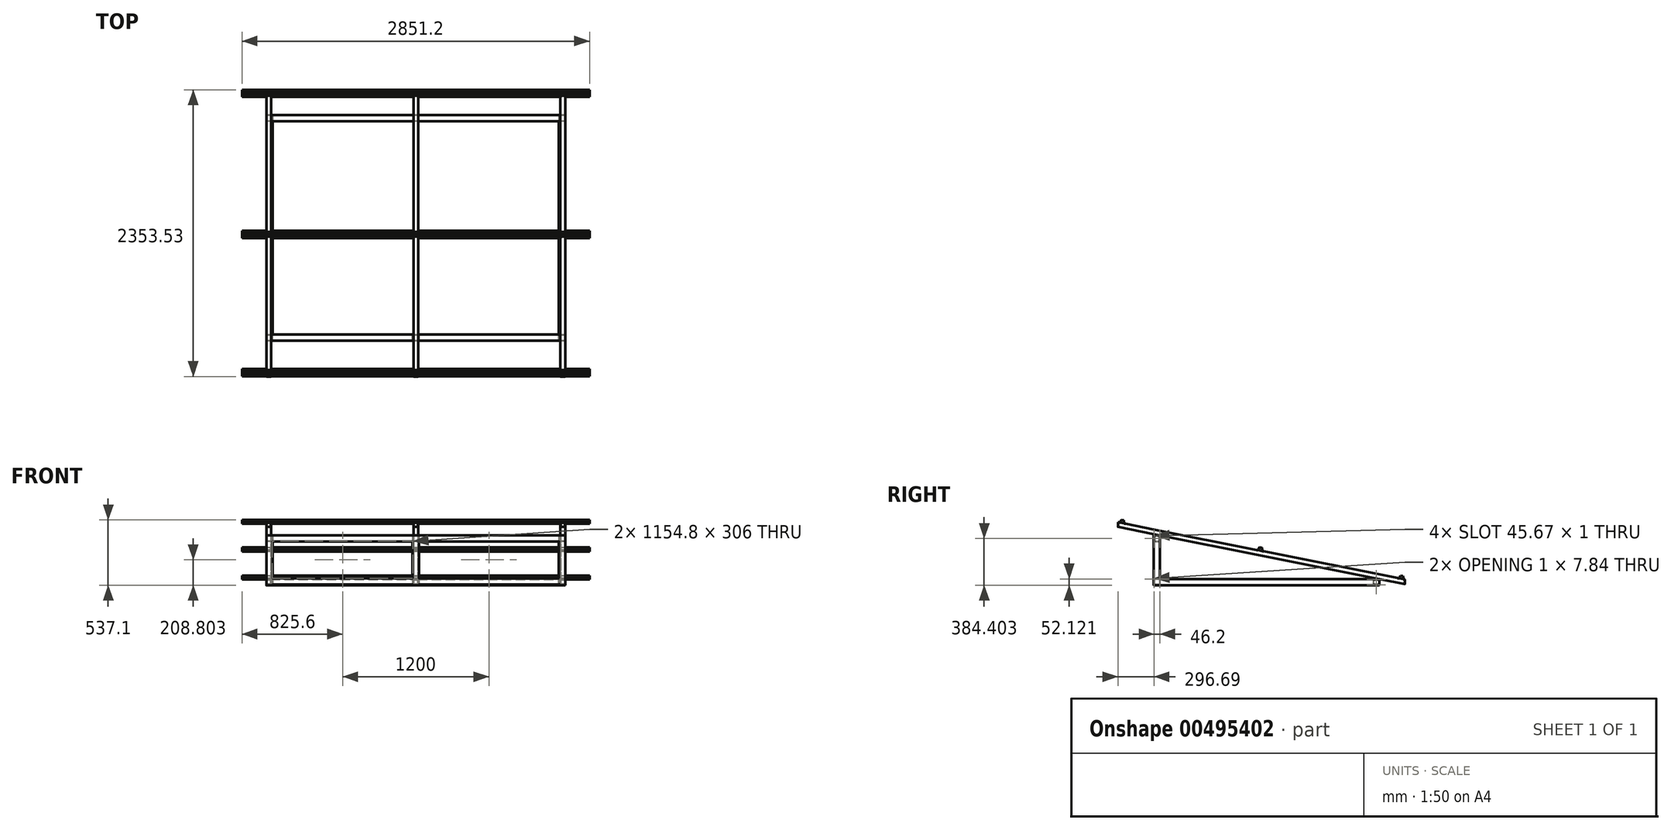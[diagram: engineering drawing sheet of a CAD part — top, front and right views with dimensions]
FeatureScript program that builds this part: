
annotation { "Feature Type Name" : "Feature", "Feature Type Description" : "" }
export const myFeature = defineFeature(function(context is Context, id is Id, definition is map)
    precondition{}
    {
        {
            var Q0;
            Q0=qCreatedBy(makeId("Front.planeOp"),FACE);
            var sketch = newSketch(context, id + "F0", { "sketchPlane" : qUnion([Q0])});
            skLineSegment(sketch, "E0.bottom", {"start": v(-48.2, -14.68) * mm, "end": v(-3, -14.68) * mm});
            skLineSegment(sketch, "E0.top", {"start": v(-48.2, 36.52) * mm, "end": v(-3, 36.52) * mm});
            skLineSegment(sketch, "E0.left", {"start": v(-51.2, -11.68) * mm, "end": v(-51.2, 33.52) * mm});
            skLineSegment(sketch, "E0.right", {"start": v(0, -11.68) * mm, "end": v(0, 33.52) * mm});
            skLineSegment(sketch, "E1.0", {"start": v(-49.2, -9.68) * mm, "end": v(-49.2, 31.52) * mm});
            skLineSegment(sketch, "E1.1", {"start": v(-46.2, -12.68) * mm, "end": v(-5, -12.68) * mm});
            skLineSegment(sketch, "E1.2", {"start": v(-2, -9.68) * mm, "end": v(-2, 31.52) * mm});
            skLineSegment(sketch, "E1.3", {"start": v(-46.2, 34.52) * mm, "end": v(-5, 34.52) * mm});
            skPoint(sketch, "E2.visualSharp", {"position": v(-49.2, 34.52) * mm});
            skArc(sketch, "E2.filletArc", {"start": v(-46.2, 34.52) * mm, "mid": v(-48.32, 33.64) * mm, "end": v(-49.2, 31.52) * mm});
            skPoint(sketch, "E3.visualSharp", {"position": v(-2, 34.52) * mm});
            skArc(sketch, "E3.filletArc", {"start": v(-2, 31.52) * mm, "mid": v(-2.88, 33.64) * mm, "end": v(-5, 34.52) * mm});
            skPoint(sketch, "E4.visualSharp", {"position": v(-2, -12.68) * mm});
            skArc(sketch, "E4.filletArc", {"start": v(-5, -12.68) * mm, "mid": v(-2.88, -11.8) * mm, "end": v(-2, -9.68) * mm});
            skPoint(sketch, "E5.visualSharp", {"position": v(-49.2, -12.68) * mm});
            skArc(sketch, "E5.filletArc", {"start": v(-49.2, -9.68) * mm, "mid": v(-48.32, -11.8) * mm, "end": v(-46.2, -12.68) * mm});
            skPoint(sketch, "E6.visualSharp", {"position": v(-51.2, -14.68) * mm});
            skArc(sketch, "E6.filletArc", {"start": v(-51.2, -11.68) * mm, "mid": v(-50.32, -13.8) * mm, "end": v(-48.2, -14.68) * mm});
            skPoint(sketch, "E7.visualSharp", {"position": v(-51.2, 36.52) * mm});
            skArc(sketch, "E7.filletArc", {"start": v(-48.2, 36.52) * mm, "mid": v(-50.32, 35.64) * mm, "end": v(-51.2, 33.52) * mm});
            skPoint(sketch, "E8.visualSharp", {"position": v(0, 36.52) * mm});
            skArc(sketch, "E8.filletArc", {"start": v(0, 33.52) * mm, "mid": v(-0.88, 35.64) * mm, "end": v(-3, 36.52) * mm});
            skPoint(sketch, "E9.visualSharp", {"position": v(0, -14.68) * mm});
            skArc(sketch, "E9.filletArc", {"start": v(-3, -14.68) * mm, "mid": v(-0.88, -13.8) * mm, "end": v(0, -11.68) * mm});
            skLineSegment(sketch, "E10", {"start": v(-51.2, 10.92) * mm, "end": v(0, 10.92) * mm});
            skLineSegment(sketch, "E11", {"start": v(-25.6, 10.92) * mm, "end": v(-25.6, 36.52) * mm});
            skLineSegment(sketch, "E12.1.0.0", {"start": v(2351.8, 36.52) * mm, "end": v(2397, 36.52) * mm});
            skArc(sketch, "E12.1.0.1", {"start": v(2400, 33.52) * mm, "mid": v(2399.12, 35.64) * mm, "end": v(2397, 36.52) * mm});
            skArc(sketch, "E12.1.0.2", {"start": v(2398, 31.52) * mm, "mid": v(2397.12, 33.64) * mm, "end": v(2395, 34.52) * mm});
            skLineSegment(sketch, "E12.1.0.3", {"start": v(2400, -11.68) * mm, "end": v(2400, 33.52) * mm});
            skLineSegment(sketch, "E12.1.0.4", {"start": v(2398, -9.68) * mm, "end": v(2398, 31.52) * mm});
            skLineSegment(sketch, "E12.1.0.5", {"start": v(2353.8, 34.52) * mm, "end": v(2395, 34.52) * mm});
            skArc(sketch, "E12.1.0.6", {"start": v(2353.8, 34.52) * mm, "mid": v(2351.68, 33.64) * mm, "end": v(2350.8, 31.52) * mm});
            skArc(sketch, "E12.1.0.7", {"start": v(2351.8, 36.52) * mm, "mid": v(2349.68, 35.64) * mm, "end": v(2348.8, 33.52) * mm});
            skLineSegment(sketch, "E12.1.0.8", {"start": v(2348.8, -11.68) * mm, "end": v(2348.8, 33.52) * mm});
            skLineSegment(sketch, "E12.1.0.9", {"start": v(2350.8, -9.68) * mm, "end": v(2350.8, 31.52) * mm});
            skArc(sketch, "E12.1.0.10", {"start": v(2350.8, -9.68) * mm, "mid": v(2351.68, -11.8) * mm, "end": v(2353.8, -12.68) * mm});
            skArc(sketch, "E12.1.0.11", {"start": v(2348.8, -11.68) * mm, "mid": v(2349.68, -13.8) * mm, "end": v(2351.8, -14.68) * mm});
            skLineSegment(sketch, "E12.1.0.12", {"start": v(2353.8, -12.68) * mm, "end": v(2395, -12.68) * mm});
            skLineSegment(sketch, "E12.1.0.13", {"start": v(2351.8, -14.68) * mm, "end": v(2397, -14.68) * mm});
            skArc(sketch, "E12.1.0.14", {"start": v(2395, -12.68) * mm, "mid": v(2397.12, -11.8) * mm, "end": v(2398, -9.68) * mm});
            skArc(sketch, "E12.1.0.15", {"start": v(2397, -14.68) * mm, "mid": v(2399.12, -13.8) * mm, "end": v(2400, -11.68) * mm});
            skLineSegment(sketch, "E12.direction1", {"start": v(-48.2, 36.52) * mm, "end": v(2351.8, 36.52) * mm, "construction": true});
            skSolve(sketch);
        }
        {
            var Q0;
            {var subQ0=sQuery(id+"F0.wireOp",EDGE,"E3.filletArc");Q0=makeQuery(id+"F0.imprint","IMPRINT",FACE,{"disambiguationData":[TD([[makeQuery(id+"F0.imprint","IMPRINT",EDGE,{"derivedFrom":subQ0}),-1.0]])]});}
            var Q1;
            {var subQ0=sQuery(id+"F0.wireOp",EDGE,"E2.filletArc");Q1=makeQuery(id+"F0.imprint","IMPRINT",FACE,{"disambiguationData":[TD([[makeQuery(id+"F0.imprint","IMPRINT",EDGE,{"derivedFrom":subQ0}),-1.0]])]});}
            var Q2;
            Q2=makeQuery(id+"F0.imprint","IMPRINT",FACE,{"disambiguationData":[TD([[makeQuery(id+"F0.imprint","IMPRINT",EDGE,{"derivedFrom":sQuery(id+"F0.wireOp",EDGE,"E0.bottom")}),1.0]])]});
            var Q3;
            Q3=makeQuery(id+"F0.imprint","IMPRINT",FACE,{"disambiguationData":[TD([[makeQuery(id+"F0.imprint","IMPRINT",EDGE,{"derivedFrom":sQuery(id+"F0.wireOp",EDGE,"E12.1.0.0")}),-1.0]])]});
            extrude(context, id + "F1", {"entities" : qUnion([Q0, Q1, Q2, Q3]), "oppositeDirection" : true, "depth" : 1851.2 * mm});
        }
        {
            var Q0;
            Q0=makeQuery(id+"F1.opExtrude","SWEPT_FACE",FACE,{"disambiguationData":[OSD([sQuery(id+"F0.wireOp",EDGE,"E0.left")])]});
            var sketch = newSketch(context, id + "F2", { "sketchPlane" : qUnion([Q0])});
            skLineSegment(sketch, "E13.bottom", {"start": v(-1848.2, -14.68) * mm, "end": v(-1803, -14.68) * mm});
            skLineSegment(sketch, "E13.top", {"start": v(-1848.2, 36.52) * mm, "end": v(-1803, 36.52) * mm});
            skLineSegment(sketch, "E13.left", {"start": v(-1851.2, -11.68) * mm, "end": v(-1851.2, 33.52) * mm});
            skLineSegment(sketch, "E13.right", {"start": v(-1800, -11.68) * mm, "end": v(-1800, 33.52) * mm});
            skLineSegment(sketch, "E14.0", {"start": v(-1849.2, -9.68) * mm, "end": v(-1849.2, 31.52) * mm});
            skLineSegment(sketch, "E14.1", {"start": v(-1846.2, -12.68) * mm, "end": v(-1805, -12.68) * mm});
            skLineSegment(sketch, "E14.2", {"start": v(-1802, -9.68) * mm, "end": v(-1802, 31.52) * mm});
            skLineSegment(sketch, "E14.3", {"start": v(-1846.2, 34.52) * mm, "end": v(-1805, 34.52) * mm});
            skPoint(sketch, "E15.visualSharp", {"position": v(-1849.2, 34.52) * mm});
            skArc(sketch, "E15.filletArc", {"start": v(-1846.2, 34.52) * mm, "mid": v(-1848.32, 33.64) * mm, "end": v(-1849.2, 31.52) * mm});
            skPoint(sketch, "E16.visualSharp", {"position": v(-1802, 34.52) * mm});
            skArc(sketch, "E16.filletArc", {"start": v(-1802, 31.52) * mm, "mid": v(-1802.88, 33.64) * mm, "end": v(-1805, 34.52) * mm});
            skPoint(sketch, "E17.visualSharp", {"position": v(-1802, -12.68) * mm});
            skArc(sketch, "E17.filletArc", {"start": v(-1805, -12.68) * mm, "mid": v(-1802.88, -11.8) * mm, "end": v(-1802, -9.68) * mm});
            skPoint(sketch, "E18.visualSharp", {"position": v(-1851.2, -14.68) * mm});
            skArc(sketch, "E18.filletArc", {"start": v(-1851.2, -11.68) * mm, "mid": v(-1850.32, -13.8) * mm, "end": v(-1848.2, -14.68) * mm});
            skPoint(sketch, "E19.visualSharp", {"position": v(-1849.2, -12.68) * mm});
            skArc(sketch, "E19.filletArc", {"start": v(-1849.2, -9.68) * mm, "mid": v(-1848.32, -11.8) * mm, "end": v(-1846.2, -12.68) * mm});
            skPoint(sketch, "E20.visualSharp", {"position": v(-1800, -14.68) * mm});
            skArc(sketch, "E20.filletArc", {"start": v(-1803, -14.68) * mm, "mid": v(-1800.88, -13.8) * mm, "end": v(-1800, -11.68) * mm});
            skPoint(sketch, "E21.visualSharp", {"position": v(-1851.2, 36.52) * mm});
            skArc(sketch, "E21.filletArc", {"start": v(-1848.2, 36.52) * mm, "mid": v(-1850.32, 35.64) * mm, "end": v(-1851.2, 33.52) * mm});
            skPoint(sketch, "E22.visualSharp", {"position": v(-1800, 36.52) * mm});
            skArc(sketch, "E22.filletArc", {"start": v(-1800, 33.52) * mm, "mid": v(-1800.88, 35.64) * mm, "end": v(-1803, 36.52) * mm});
            skSolve(sketch);
        }
        {
            var Q0;
            Q0 = qSketchRegion(id + "F2", true);
            extrude(context, id + "F3", {"entities" : qUnion([Q0]), "operationType" : NewBodyOperationType.ADD, "oppositeDirection" : true, "depth" : 2451.2 * mm});
        }
        {
            var Q0;
            Q0=makeQuery(id+"F3.boolean.opBoolean","MERGE",FACE,{"derivedFrom":[makeQuery(id+"F1.opExtrude","SWEPT_FACE",FACE,{"disambiguationData":[OSD([sQuery(id+"F0.wireOp",EDGE,"E0.bottom")])]}),makeQuery(id+"F3.opExtrude","SWEPT_FACE",FACE,{"disambiguationData":[OSD([sQuery(id+"F2.wireOp",EDGE,"E13.bottom")])]})]});
            var sketch = newSketch(context, id + "F4", { "sketchPlane" : qUnion([Q0])});
            skLineSegment(sketch, "E23.bottom", {"start": v(-48.2, -51.2) * mm, "end": v(-3, -51.2) * mm});
            skLineSegment(sketch, "E23.top", {"start": v(-48.2, 0) * mm, "end": v(-3, 0) * mm});
            skLineSegment(sketch, "E23.left", {"start": v(-51.2, -48.2) * mm, "end": v(-51.2, -3) * mm});
            skLineSegment(sketch, "E23.right", {"start": v(0, -48.2) * mm, "end": v(0, -3) * mm});
            skLineSegment(sketch, "E24.0", {"start": v(-49.2, -46.2) * mm, "end": v(-49.2, -5) * mm});
            skLineSegment(sketch, "E24.1", {"start": v(-46.2, -49.2) * mm, "end": v(-5, -49.2) * mm});
            skLineSegment(sketch, "E24.2", {"start": v(-2, -46.2) * mm, "end": v(-2, -5) * mm});
            skLineSegment(sketch, "E24.3", {"start": v(-46.2, -2) * mm, "end": v(-5, -2) * mm});
            skPoint(sketch, "E25.visualSharp", {"position": v(-49.2, -2) * mm});
            skArc(sketch, "E25.filletArc", {"start": v(-46.2, -2) * mm, "mid": v(-48.32, -2.88) * mm, "end": v(-49.2, -5) * mm});
            skPoint(sketch, "E26.visualSharp", {"position": v(-2, -2) * mm});
            skArc(sketch, "E26.filletArc", {"start": v(-2, -5) * mm, "mid": v(-2.88, -2.88) * mm, "end": v(-5, -2) * mm});
            skPoint(sketch, "E27.visualSharp", {"position": v(-2, -49.2) * mm});
            skArc(sketch, "E27.filletArc", {"start": v(-5, -49.2) * mm, "mid": v(-2.88, -48.32) * mm, "end": v(-2, -46.2) * mm});
            skPoint(sketch, "E28.visualSharp", {"position": v(-49.2, -49.2) * mm});
            skArc(sketch, "E28.filletArc", {"start": v(-49.2, -46.2) * mm, "mid": v(-48.32, -48.32) * mm, "end": v(-46.2, -49.2) * mm});
            skPoint(sketch, "E29.visualSharp", {"position": v(-51.2, -51.2) * mm});
            skArc(sketch, "E29.filletArc", {"start": v(-51.2, -48.2) * mm, "mid": v(-50.32, -50.32) * mm, "end": v(-48.2, -51.2) * mm});
            skPoint(sketch, "E30.visualSharp", {"position": v(-51.2, 0) * mm});
            skArc(sketch, "E30.filletArc", {"start": v(-48.2, 0) * mm, "mid": v(-50.32, -0.88) * mm, "end": v(-51.2, -3) * mm});
            skPoint(sketch, "E31.visualSharp", {"position": v(0, 0) * mm});
            skArc(sketch, "E31.filletArc", {"start": v(0, -3) * mm, "mid": v(-0.88, -0.88) * mm, "end": v(-3, 0) * mm});
            skPoint(sketch, "E32.visualSharp", {"position": v(0, -51.2) * mm});
            skArc(sketch, "E32.filletArc", {"start": v(-3, -51.2) * mm, "mid": v(-0.88, -50.32) * mm, "end": v(0, -48.2) * mm});
            skLineSegment(sketch, "E33.1.0.0", {"start": v(2351.8, 0) * mm, "end": v(2397, 0) * mm});
            skLineSegment(sketch, "E33.1.0.1", {"start": v(2353.8, -2) * mm, "end": v(2395, -2) * mm});
            skArc(sketch, "E33.1.0.2", {"start": v(2400, -3) * mm, "mid": v(2399.12, -0.88) * mm, "end": v(2397, 0) * mm});
            skArc(sketch, "E33.1.0.3", {"start": v(2398, -5) * mm, "mid": v(2397.12, -2.88) * mm, "end": v(2395, -2) * mm});
            skArc(sketch, "E33.1.0.4", {"start": v(2353.8, -2) * mm, "mid": v(2351.68, -2.88) * mm, "end": v(2350.8, -5) * mm});
            skArc(sketch, "E33.1.0.5", {"start": v(2351.8, 0) * mm, "mid": v(2349.68, -0.88) * mm, "end": v(2348.8, -3) * mm});
            skLineSegment(sketch, "E33.1.0.6", {"start": v(2348.8, -48.2) * mm, "end": v(2348.8, -3) * mm});
            skLineSegment(sketch, "E33.1.0.7", {"start": v(2350.8, -46.2) * mm, "end": v(2350.8, -5) * mm});
            skArc(sketch, "E33.1.0.8", {"start": v(2350.8, -46.2) * mm, "mid": v(2351.68, -48.32) * mm, "end": v(2353.8, -49.2) * mm});
            skArc(sketch, "E33.1.0.9", {"start": v(2348.8, -48.2) * mm, "mid": v(2349.68, -50.32) * mm, "end": v(2351.8, -51.2) * mm});
            skLineSegment(sketch, "E33.1.0.10", {"start": v(2353.8, -49.2) * mm, "end": v(2395, -49.2) * mm});
            skLineSegment(sketch, "E33.1.0.11", {"start": v(2351.8, -51.2) * mm, "end": v(2397, -51.2) * mm});
            skArc(sketch, "E33.1.0.12", {"start": v(2395, -49.2) * mm, "mid": v(2397.12, -48.32) * mm, "end": v(2398, -46.2) * mm});
            skArc(sketch, "E33.1.0.13", {"start": v(2397, -51.2) * mm, "mid": v(2399.12, -50.32) * mm, "end": v(2400, -48.2) * mm});
            skLineSegment(sketch, "E33.1.0.14", {"start": v(2400, -48.2) * mm, "end": v(2400, -3) * mm});
            skLineSegment(sketch, "E33.1.0.15", {"start": v(2398, -46.2) * mm, "end": v(2398, -5) * mm});
            skLineSegment(sketch, "E33.direction1", {"start": v(-48.2, 0) * mm, "end": v(2351.8, 0) * mm, "construction": true});
            skLineSegment(sketch, "E34.bottom", {"start": v(1151.8, -51.2) * mm, "end": v(1197, -51.2) * mm});
            skLineSegment(sketch, "E34.top", {"start": v(1151.8, 0) * mm, "end": v(1197, 0) * mm});
            skLineSegment(sketch, "E34.left", {"start": v(1148.8, -48.2) * mm, "end": v(1148.8, -3) * mm});
            skLineSegment(sketch, "E34.right", {"start": v(1200, -48.2) * mm, "end": v(1200, -3) * mm});
            skLineSegment(sketch, "E35.0", {"start": v(1150.8, -46.2) * mm, "end": v(1150.8, -5) * mm});
            skLineSegment(sketch, "E35.1", {"start": v(1153.8, -49.2) * mm, "end": v(1195, -49.2) * mm});
            skLineSegment(sketch, "E35.2", {"start": v(1198, -46.2) * mm, "end": v(1198, -5) * mm});
            skLineSegment(sketch, "E35.3", {"start": v(1153.8, -2) * mm, "end": v(1195, -2) * mm});
            skPoint(sketch, "E36.visualSharp", {"position": v(1150.8, -2) * mm});
            skArc(sketch, "E36.filletArc", {"start": v(1153.8, -2) * mm, "mid": v(1151.68, -2.88) * mm, "end": v(1150.8, -5) * mm});
            skPoint(sketch, "E37.visualSharp", {"position": v(1198, -2) * mm});
            skArc(sketch, "E37.filletArc", {"start": v(1198, -5) * mm, "mid": v(1197.12, -2.88) * mm, "end": v(1195, -2) * mm});
            skPoint(sketch, "E38.visualSharp", {"position": v(1198, -49.2) * mm});
            skArc(sketch, "E38.filletArc", {"start": v(1195, -49.2) * mm, "mid": v(1197.12, -48.32) * mm, "end": v(1198, -46.2) * mm});
            skPoint(sketch, "E39.visualSharp", {"position": v(1150.8, -49.2) * mm});
            skArc(sketch, "E39.filletArc", {"start": v(1150.8, -46.2) * mm, "mid": v(1151.68, -48.32) * mm, "end": v(1153.8, -49.2) * mm});
            skPoint(sketch, "E40.visualSharp", {"position": v(1148.8, -51.2) * mm});
            skArc(sketch, "E40.filletArc", {"start": v(1148.8, -48.2) * mm, "mid": v(1149.68, -50.32) * mm, "end": v(1151.8, -51.2) * mm});
            skPoint(sketch, "E41.visualSharp", {"position": v(1148.8, 0) * mm});
            skArc(sketch, "E41.filletArc", {"start": v(1151.8, 0) * mm, "mid": v(1149.68, -0.88) * mm, "end": v(1148.8, -3) * mm});
            skPoint(sketch, "E42.visualSharp", {"position": v(1200, 0) * mm});
            skArc(sketch, "E42.filletArc", {"start": v(1200, -3) * mm, "mid": v(1199.12, -0.88) * mm, "end": v(1197, 0) * mm});
            skPoint(sketch, "E43.visualSharp", {"position": v(1200, -51.2) * mm});
            skArc(sketch, "E43.filletArc", {"start": v(1197, -51.2) * mm, "mid": v(1199.12, -50.32) * mm, "end": v(1200, -48.2) * mm});
            skSolve(sketch);
        }
        {
            var Q0;
            Q0 = qSketchRegion(id + "F4", true);
            extrude(context, id + "F5", {"entities" : qUnion([Q0]), "oppositeDirection" : true, "depth" : 410 * mm});
        }
        {
            var Q0;
            Q0=makeQuery(id+"F1.opExtrude","SWEPT_BODY",BODY,{"disambiguationData":[OSD([sQuery(id+"F0.wireOp",EDGE,"E0.bottom"),sQuery(id+"F0.wireOp",EDGE,"E0.top"),sQuery(id+"F0.wireOp",EDGE,"E0.left"),sQuery(id+"F0.wireOp",EDGE,"E0.right"),sQuery(id+"F0.wireOp",EDGE,"E1.0"),sQuery(id+"F0.wireOp",EDGE,"E1.1"),sQuery(id+"F0.wireOp",EDGE,"E1.2"),sQuery(id+"F0.wireOp",EDGE,"E1.3"),sQuery(id+"F0.wireOp",EDGE,"E2.filletArc"),sQuery(id+"F0.wireOp",EDGE,"E3.filletArc"),sQuery(id+"F0.wireOp",EDGE,"E4.filletArc"),sQuery(id+"F0.wireOp",EDGE,"E5.filletArc"),sQuery(id+"F0.wireOp",EDGE,"E6.filletArc"),sQuery(id+"F0.wireOp",EDGE,"E7.filletArc"),sQuery(id+"F0.wireOp",EDGE,"E8.filletArc"),sQuery(id+"F0.wireOp",EDGE,"E9.filletArc")])]});
            var Q1;
            Q1=makeQuery(id+"F1.opExtrude","SWEPT_BODY",BODY,{"disambiguationData":[OSD([sQuery(id+"F0.wireOp",EDGE,"E12.1.0.0"),sQuery(id+"F0.wireOp",EDGE,"E12.1.0.1"),sQuery(id+"F0.wireOp",EDGE,"E12.1.0.2"),sQuery(id+"F0.wireOp",EDGE,"E12.1.0.3"),sQuery(id+"F0.wireOp",EDGE,"E12.1.0.4"),sQuery(id+"F0.wireOp",EDGE,"E12.1.0.5"),sQuery(id+"F0.wireOp",EDGE,"E12.1.0.6"),sQuery(id+"F0.wireOp",EDGE,"E12.1.0.7"),sQuery(id+"F0.wireOp",EDGE,"E12.1.0.8"),sQuery(id+"F0.wireOp",EDGE,"E12.1.0.9"),sQuery(id+"F0.wireOp",EDGE,"E12.1.0.10"),sQuery(id+"F0.wireOp",EDGE,"E12.1.0.11"),sQuery(id+"F0.wireOp",EDGE,"E12.1.0.12"),sQuery(id+"F0.wireOp",EDGE,"E12.1.0.13"),sQuery(id+"F0.wireOp",EDGE,"E12.1.0.14"),sQuery(id+"F0.wireOp",EDGE,"E12.1.0.15")])]});
            var Q2;
            Q2=makeQuery(id+"F5.opExtrude","SWEPT_BODY",BODY,{"disambiguationData":[OSD([sQuery(id+"F4.wireOp",EDGE,"E23.bottom"),sQuery(id+"F4.wireOp",EDGE,"E23.top"),sQuery(id+"F4.wireOp",EDGE,"E23.left"),sQuery(id+"F4.wireOp",EDGE,"E23.right"),sQuery(id+"F4.wireOp",EDGE,"E24.0"),sQuery(id+"F4.wireOp",EDGE,"E24.1"),sQuery(id+"F4.wireOp",EDGE,"E24.2"),sQuery(id+"F4.wireOp",EDGE,"E24.3"),sQuery(id+"F4.wireOp",EDGE,"E25.filletArc"),sQuery(id+"F4.wireOp",EDGE,"E26.filletArc"),sQuery(id+"F4.wireOp",EDGE,"E27.filletArc"),sQuery(id+"F4.wireOp",EDGE,"E28.filletArc"),sQuery(id+"F4.wireOp",EDGE,"E29.filletArc"),sQuery(id+"F4.wireOp",EDGE,"E30.filletArc"),sQuery(id+"F4.wireOp",EDGE,"E31.filletArc"),sQuery(id+"F4.wireOp",EDGE,"E32.filletArc")])]});
            var Q3;
            Q3=makeQuery(id+"F5.opExtrude","SWEPT_BODY",BODY,{"disambiguationData":[OSD([sQuery(id+"F4.wireOp",EDGE,"E33.1.0.0"),sQuery(id+"F4.wireOp",EDGE,"E33.1.0.1"),sQuery(id+"F4.wireOp",EDGE,"E33.1.0.2"),sQuery(id+"F4.wireOp",EDGE,"E33.1.0.3"),sQuery(id+"F4.wireOp",EDGE,"E33.1.0.4"),sQuery(id+"F4.wireOp",EDGE,"E33.1.0.5"),sQuery(id+"F4.wireOp",EDGE,"E33.1.0.6"),sQuery(id+"F4.wireOp",EDGE,"E33.1.0.7"),sQuery(id+"F4.wireOp",EDGE,"E33.1.0.8"),sQuery(id+"F4.wireOp",EDGE,"E33.1.0.9"),sQuery(id+"F4.wireOp",EDGE,"E33.1.0.10"),sQuery(id+"F4.wireOp",EDGE,"E33.1.0.11"),sQuery(id+"F4.wireOp",EDGE,"E33.1.0.12"),sQuery(id+"F4.wireOp",EDGE,"E33.1.0.13"),sQuery(id+"F4.wireOp",EDGE,"E33.1.0.14"),sQuery(id+"F4.wireOp",EDGE,"E33.1.0.15")])]});
            booleanBodies(context, id + "F6", {"operationType" : BooleanOperationType.UNION, "tools" : qUnion([Q0, Q1, Q2, Q3])});
        }
        {
            var Q0;
            Q0=makeQuery(id+"F6.opBoolean","MERGE",FACE,{"derivedFrom":[makeQuery(id+"F3.boolean.opBoolean","MERGE",FACE,{"derivedFrom":[makeQuery(id+"F1.opExtrude","SWEPT_FACE",FACE,{"disambiguationData":[OSD([sQuery(id+"F0.wireOp",EDGE,"E0.left")])]}),makeQuery(id+"F3.opExtrude","CAP_FACE",FACE,{"disambiguationData":[OSD([sQuery(id+"F2.wireOp",EDGE,"E13.bottom"),sQuery(id+"F2.wireOp",EDGE,"E13.top"),sQuery(id+"F2.wireOp",EDGE,"E13.left"),sQuery(id+"F2.wireOp",EDGE,"E13.right"),sQuery(id+"F2.wireOp",EDGE,"E14.0"),sQuery(id+"F2.wireOp",EDGE,"E14.1"),sQuery(id+"F2.wireOp",EDGE,"E14.2"),sQuery(id+"F2.wireOp",EDGE,"E14.3"),sQuery(id+"F2.wireOp",EDGE,"E15.filletArc"),sQuery(id+"F2.wireOp",EDGE,"E16.filletArc"),sQuery(id+"F2.wireOp",EDGE,"E17.filletArc"),sQuery(id+"F2.wireOp",EDGE,"E18.filletArc"),sQuery(id+"F2.wireOp",EDGE,"E19.filletArc"),sQuery(id+"F2.wireOp",EDGE,"E20.filletArc"),sQuery(id+"F2.wireOp",EDGE,"E21.filletArc"),sQuery(id+"F2.wireOp",EDGE,"E22.filletArc")])],"isStart":true})]}),makeQuery(id+"F5.opExtrude","SWEPT_FACE",FACE,{"disambiguationData":[OSD([sQuery(id+"F4.wireOp",EDGE,"E23.left")])]})]});
            var sketch = newSketch(context, id + "F7", { "sketchPlane" : qUnion([Q0])});
            skLineSegment(sketch, "E44.bottom", {"start": v(-48.2, 344.12) * mm, "end": v(-3, 344.12) * mm});
            skLineSegment(sketch, "E44.top", {"start": v(-48.2, 395.32) * mm, "end": v(-3, 395.32) * mm});
            skLineSegment(sketch, "E44.left", {"start": v(-51.2, 347.12) * mm, "end": v(-51.2, 392.32) * mm});
            skLineSegment(sketch, "E44.right", {"start": v(0, 347.12) * mm, "end": v(0, 392.32) * mm});
            skLineSegment(sketch, "E45.0", {"start": v(-49.2, 349.12) * mm, "end": v(-49.2, 390.32) * mm});
            skLineSegment(sketch, "E45.1", {"start": v(-46.2, 346.12) * mm, "end": v(-5, 346.12) * mm});
            skLineSegment(sketch, "E45.2", {"start": v(-2, 349.12) * mm, "end": v(-2, 390.32) * mm});
            skLineSegment(sketch, "E45.3", {"start": v(-46.2, 393.32) * mm, "end": v(-5, 393.32) * mm});
            skPoint(sketch, "E46.visualSharp", {"position": v(-49.2, 393.32) * mm});
            skArc(sketch, "E46.filletArc", {"start": v(-46.2, 393.32) * mm, "mid": v(-48.32, 392.44) * mm, "end": v(-49.2, 390.32) * mm});
            skPoint(sketch, "E47.visualSharp", {"position": v(-2, 393.32) * mm});
            skArc(sketch, "E47.filletArc", {"start": v(-2, 390.32) * mm, "mid": v(-2.88, 392.44) * mm, "end": v(-5, 393.32) * mm});
            skPoint(sketch, "E48.visualSharp", {"position": v(-2, 346.12) * mm});
            skArc(sketch, "E48.filletArc", {"start": v(-5, 346.12) * mm, "mid": v(-2.88, 347) * mm, "end": v(-2, 349.12) * mm});
            skPoint(sketch, "E49.visualSharp", {"position": v(-49.2, 346.12) * mm});
            skArc(sketch, "E49.filletArc", {"start": v(-49.2, 349.12) * mm, "mid": v(-48.32, 347) * mm, "end": v(-46.2, 346.12) * mm});
            skPoint(sketch, "E50.visualSharp", {"position": v(-51.2, 344.12) * mm});
            skArc(sketch, "E50.filletArc", {"start": v(-51.2, 347.12) * mm, "mid": v(-50.32, 345) * mm, "end": v(-48.2, 344.12) * mm});
            skPoint(sketch, "E51.visualSharp", {"position": v(-51.2, 395.32) * mm});
            skArc(sketch, "E51.filletArc", {"start": v(-48.2, 395.32) * mm, "mid": v(-50.32, 394.44) * mm, "end": v(-51.2, 392.32) * mm});
            skPoint(sketch, "E52.visualSharp", {"position": v(0, 395.32) * mm});
            skArc(sketch, "E52.filletArc", {"start": v(0, 392.32) * mm, "mid": v(-0.88, 394.44) * mm, "end": v(-3, 395.32) * mm});
            skPoint(sketch, "E53.visualSharp", {"position": v(0, 344.12) * mm});
            skArc(sketch, "E53.filletArc", {"start": v(-3, 344.12) * mm, "mid": v(-0.88, 345) * mm, "end": v(0, 347.12) * mm});
            skLineSegment(sketch, "E54.0.1.0", {"start": v(0, -4.08) * mm, "end": v(0, 41.12) * mm});
            skLineSegment(sketch, "E54.0.1.1", {"start": v(-48.2, -7.08) * mm, "end": v(-3, -7.08) * mm});
            skLineSegment(sketch, "E54.direction1", {"start": v(0, 347.12) * mm, "end": v(25, 347.12) * mm, "construction": true});
            skLineSegment(sketch, "E54.direction2", {"start": v(0, 347.12) * mm, "end": v(0, -4.08) * mm, "construction": true});
            skLineSegment(sketch, "E55.top", {"start": v(-48.2, 44.12) * mm, "end": v(-3, 44.12) * mm});
            skLineSegment(sketch, "E55.left", {"start": v(-51.2, -4.08) * mm, "end": v(-51.2, 41.12) * mm});
            skLineSegment(sketch, "E56.0", {"start": v(-49.2, -2.08) * mm, "end": v(-49.2, 39.12) * mm});
            skLineSegment(sketch, "E56.1", {"start": v(-46.2, -5.08) * mm, "end": v(-5, -5.08) * mm});
            skLineSegment(sketch, "E56.2", {"start": v(-2, -2.08) * mm, "end": v(-2, 39.12) * mm});
            skLineSegment(sketch, "E56.3", {"start": v(-46.2, 42.12) * mm, "end": v(-5, 42.12) * mm});
            skPoint(sketch, "E57.visualSharp", {"position": v(-49.2, 42.12) * mm});
            skArc(sketch, "E57.filletArc", {"start": v(-46.2, 42.12) * mm, "mid": v(-48.32, 41.24) * mm, "end": v(-49.2, 39.12) * mm});
            skPoint(sketch, "E58.visualSharp", {"position": v(-2, 42.12) * mm});
            skArc(sketch, "E58.filletArc", {"start": v(-2, 39.12) * mm, "mid": v(-2.88, 41.24) * mm, "end": v(-5, 42.12) * mm});
            skPoint(sketch, "E59.visualSharp", {"position": v(-2, -5.08) * mm});
            skArc(sketch, "E59.filletArc", {"start": v(-5, -5.08) * mm, "mid": v(-2.88, -4.2) * mm, "end": v(-2, -2.08) * mm});
            skPoint(sketch, "E60.visualSharp", {"position": v(-49.2, -5.08) * mm});
            skArc(sketch, "E60.filletArc", {"start": v(-49.2, -2.08) * mm, "mid": v(-48.32, -4.2) * mm, "end": v(-46.2, -5.08) * mm});
            skPoint(sketch, "E61.visualSharp", {"position": v(-51.2, -7.08) * mm});
            skArc(sketch, "E61.filletArc", {"start": v(-51.2, -4.08) * mm, "mid": v(-50.32, -6.2) * mm, "end": v(-48.2, -7.08) * mm});
            skPoint(sketch, "E62.visualSharp", {"position": v(-51.2, 44.12) * mm});
            skArc(sketch, "E62.filletArc", {"start": v(-48.2, 44.12) * mm, "mid": v(-50.32, 43.24) * mm, "end": v(-51.2, 41.12) * mm});
            skPoint(sketch, "E63.visualSharp", {"position": v(0, 44.12) * mm});
            skArc(sketch, "E63.filletArc", {"start": v(0, 41.12) * mm, "mid": v(-0.88, 43.24) * mm, "end": v(-3, 44.12) * mm});
            skPoint(sketch, "E64.visualSharp", {"position": v(0, -7.08) * mm});
            skArc(sketch, "E64.filletArc", {"start": v(-3, -7.08) * mm, "mid": v(-0.88, -6.2) * mm, "end": v(0, -4.08) * mm});
            skLineSegment(sketch, "E65.direction1", {"start": v(-5.85, 225.79) * mm, "end": v(19.15, 225.79) * mm, "construction": true});
            skSolve(sketch);
        }
        {
            var Q0;
            Q0 = qSketchRegion(id + "F7", true);
            var Q1;
            Q1=makeQuery(id+"F6.opBoolean","MERGE",FACE,{"derivedFrom":[makeQuery(id+"F1.opExtrude","SWEPT_FACE",FACE,{"disambiguationData":[OSD([sQuery(id+"F0.wireOp",EDGE,"E12.1.0.3")])]}),makeQuery(id+"F3.opExtrude","CAP_FACE",FACE,{"disambiguationData":[OSD([sQuery(id+"F2.wireOp",EDGE,"E13.bottom"),sQuery(id+"F2.wireOp",EDGE,"E13.top"),sQuery(id+"F2.wireOp",EDGE,"E13.left"),sQuery(id+"F2.wireOp",EDGE,"E13.right"),sQuery(id+"F2.wireOp",EDGE,"E14.0"),sQuery(id+"F2.wireOp",EDGE,"E14.1"),sQuery(id+"F2.wireOp",EDGE,"E14.2"),sQuery(id+"F2.wireOp",EDGE,"E14.3"),sQuery(id+"F2.wireOp",EDGE,"E15.filletArc"),sQuery(id+"F2.wireOp",EDGE,"E16.filletArc"),sQuery(id+"F2.wireOp",EDGE,"E17.filletArc"),sQuery(id+"F2.wireOp",EDGE,"E18.filletArc"),sQuery(id+"F2.wireOp",EDGE,"E19.filletArc"),sQuery(id+"F2.wireOp",EDGE,"E20.filletArc"),sQuery(id+"F2.wireOp",EDGE,"E21.filletArc"),sQuery(id+"F2.wireOp",EDGE,"E22.filletArc")])],"isStart":false}),makeQuery(id+"F5.opExtrude","SWEPT_FACE",FACE,{"disambiguationData":[OSD([sQuery(id+"F4.wireOp",EDGE,"E33.1.0.14")])]})]});
            extrude(context, id + "F8", {"entities" : qUnion([Q0]), "operationType" : NewBodyOperationType.ADD, "endBound" : BoundingType.UP_TO_SURFACE, "oppositeDirection" : true, "endBoundEntityFace" : qUnion([Q1]), "depth" : 25 * mm});
        }
        {
            var Q0;
            Q0=makeQuery(id+"F8.boolean.opBoolean","MERGE",FACE,{"derivedFrom":[makeQuery(id+"F6.opBoolean","MERGE",FACE,{"derivedFrom":[makeQuery(id+"F3.boolean.opBoolean","MERGE",FACE,{"derivedFrom":[makeQuery(id+"F1.opExtrude","SWEPT_FACE",FACE,{"disambiguationData":[OSD([sQuery(id+"F0.wireOp",EDGE,"E0.left")])]}),makeQuery(id+"F3.opExtrude","CAP_FACE",FACE,{"disambiguationData":[OSD([sQuery(id+"F2.wireOp",EDGE,"E13.bottom"),sQuery(id+"F2.wireOp",EDGE,"E13.top"),sQuery(id+"F2.wireOp",EDGE,"E13.left"),sQuery(id+"F2.wireOp",EDGE,"E13.right"),sQuery(id+"F2.wireOp",EDGE,"E14.0"),sQuery(id+"F2.wireOp",EDGE,"E14.1"),sQuery(id+"F2.wireOp",EDGE,"E14.2"),sQuery(id+"F2.wireOp",EDGE,"E14.3"),sQuery(id+"F2.wireOp",EDGE,"E15.filletArc"),sQuery(id+"F2.wireOp",EDGE,"E16.filletArc"),sQuery(id+"F2.wireOp",EDGE,"E17.filletArc"),sQuery(id+"F2.wireOp",EDGE,"E18.filletArc"),sQuery(id+"F2.wireOp",EDGE,"E19.filletArc"),sQuery(id+"F2.wireOp",EDGE,"E20.filletArc"),sQuery(id+"F2.wireOp",EDGE,"E21.filletArc"),sQuery(id+"F2.wireOp",EDGE,"E22.filletArc")])],"isStart":true})]}),makeQuery(id+"F5.opExtrude","SWEPT_FACE",FACE,{"disambiguationData":[OSD([sQuery(id+"F4.wireOp",EDGE,"E23.left")])]})]}),makeQuery(id+"F8.opExtrude","CAP_FACE",FACE,{"disambiguationData":[OSD([sQuery(id+"F7.wireOp",EDGE,"E44.bottom"),sQuery(id+"F7.wireOp",EDGE,"E44.top"),sQuery(id+"F7.wireOp",EDGE,"E44.left"),sQuery(id+"F7.wireOp",EDGE,"E44.right"),sQuery(id+"F7.wireOp",EDGE,"E45.0"),sQuery(id+"F7.wireOp",EDGE,"E45.1"),sQuery(id+"F7.wireOp",EDGE,"E45.2"),sQuery(id+"F7.wireOp",EDGE,"E45.3"),sQuery(id+"F7.wireOp",EDGE,"E46.filletArc"),sQuery(id+"F7.wireOp",EDGE,"E47.filletArc"),sQuery(id+"F7.wireOp",EDGE,"E48.filletArc"),sQuery(id+"F7.wireOp",EDGE,"E49.filletArc"),sQuery(id+"F7.wireOp",EDGE,"E50.filletArc"),sQuery(id+"F7.wireOp",EDGE,"E51.filletArc"),sQuery(id+"F7.wireOp",EDGE,"E52.filletArc"),sQuery(id+"F7.wireOp",EDGE,"E53.filletArc")])],"isStart":true}),makeQuery(id+"F8.opExtrude","CAP_FACE",FACE,{"disambiguationData":[OSD([sQuery(id+"F7.wireOp",EDGE,"E54.0.1.1"),sQuery(id+"F7.wireOp",EDGE,"E55.top"),sQuery(id+"F7.wireOp",EDGE,"E55.left"),sQuery(id+"F7.wireOp",EDGE,"E54.0.1.0"),sQuery(id+"F7.wireOp",EDGE,"E56.0"),sQuery(id+"F7.wireOp",EDGE,"E56.1"),sQuery(id+"F7.wireOp",EDGE,"E56.2"),sQuery(id+"F7.wireOp",EDGE,"E56.3"),sQuery(id+"F7.wireOp",EDGE,"E57.filletArc"),sQuery(id+"F7.wireOp",EDGE,"E58.filletArc"),sQuery(id+"F7.wireOp",EDGE,"E59.filletArc"),sQuery(id+"F7.wireOp",EDGE,"E60.filletArc"),sQuery(id+"F7.wireOp",EDGE,"E61.filletArc"),sQuery(id+"F7.wireOp",EDGE,"E62.filletArc"),sQuery(id+"F7.wireOp",EDGE,"E63.filletArc"),sQuery(id+"F7.wireOp",EDGE,"E64.filletArc")])],"isStart":true})]});
            var sketch = newSketch(context, id + "F9", { "sketchPlane" : qUnion([Q0])});
            skLineSegment(sketch, "E66", {"start": v(300, 465.5) * mm, "end": v(-2051.03, -4) * mm});
            skLineSegment(sketch, "E67", {"start": v(-51.2, 395.32) * mm, "end": v(-51.2, 44.12) * mm});
            skCircle(sketch, "E68", {"center": v(-51.2, 393.53) * mm, "radius": 1.79 * mm});
            skCircle(sketch, "E69", {"center": v(-1848.44, 33.52) * mm, "radius": 2.88 * mm});
            skLineSegment(sketch, "E70.0", {"start": v(0, 425.16) * mm, "end": v(-2059.34, 13.92) * mm});
            skLineSegment(sketch, "E71", {"start": v(0, 379.13) * mm, "end": v(0, 439.67) * mm});
            skLineSegment(sketch, "E72", {"start": v(0, 425.16) * mm, "end": v(294.2, 483.91) * mm});
            skSolve(sketch);
        }
        {
            var Q0;
            Q0=makeQuery(id+"F8.boolean.opBoolean","MERGE",FACE,{"derivedFrom":[makeQuery(id+"F6.opBoolean","MERGE",FACE,{"derivedFrom":[makeQuery(id+"F1.opExtrude","CAP_FACE",FACE,{"disambiguationData":[OSD([sQuery(id+"F0.wireOp",EDGE,"E0.bottom"),sQuery(id+"F0.wireOp",EDGE,"E0.top"),sQuery(id+"F0.wireOp",EDGE,"E0.left"),sQuery(id+"F0.wireOp",EDGE,"E0.right"),sQuery(id+"F0.wireOp",EDGE,"E1.0"),sQuery(id+"F0.wireOp",EDGE,"E1.1"),sQuery(id+"F0.wireOp",EDGE,"E1.2"),sQuery(id+"F0.wireOp",EDGE,"E1.3"),sQuery(id+"F0.wireOp",EDGE,"E2.filletArc"),sQuery(id+"F0.wireOp",EDGE,"E3.filletArc"),sQuery(id+"F0.wireOp",EDGE,"E4.filletArc"),sQuery(id+"F0.wireOp",EDGE,"E5.filletArc"),sQuery(id+"F0.wireOp",EDGE,"E6.filletArc"),sQuery(id+"F0.wireOp",EDGE,"E7.filletArc"),sQuery(id+"F0.wireOp",EDGE,"E8.filletArc"),sQuery(id+"F0.wireOp",EDGE,"E9.filletArc")])],"isStart":true}),makeQuery(id+"F5.opExtrude","SWEPT_FACE",FACE,{"disambiguationData":[OSD([sQuery(id+"F4.wireOp",EDGE,"E23.top")])]})]}),makeQuery(id+"F6.opBoolean","MERGE",FACE,{"derivedFrom":[makeQuery(id+"F1.opExtrude","CAP_FACE",FACE,{"disambiguationData":[OSD([sQuery(id+"F0.wireOp",EDGE,"E12.1.0.0"),sQuery(id+"F0.wireOp",EDGE,"E12.1.0.1"),sQuery(id+"F0.wireOp",EDGE,"E12.1.0.2"),sQuery(id+"F0.wireOp",EDGE,"E12.1.0.3"),sQuery(id+"F0.wireOp",EDGE,"E12.1.0.4"),sQuery(id+"F0.wireOp",EDGE,"E12.1.0.5"),sQuery(id+"F0.wireOp",EDGE,"E12.1.0.6"),sQuery(id+"F0.wireOp",EDGE,"E12.1.0.7"),sQuery(id+"F0.wireOp",EDGE,"E12.1.0.8"),sQuery(id+"F0.wireOp",EDGE,"E12.1.0.9"),sQuery(id+"F0.wireOp",EDGE,"E12.1.0.10"),sQuery(id+"F0.wireOp",EDGE,"E12.1.0.11"),sQuery(id+"F0.wireOp",EDGE,"E12.1.0.12"),sQuery(id+"F0.wireOp",EDGE,"E12.1.0.13"),sQuery(id+"F0.wireOp",EDGE,"E12.1.0.14"),sQuery(id+"F0.wireOp",EDGE,"E12.1.0.15")])],"isStart":true}),makeQuery(id+"F5.opExtrude","SWEPT_FACE",FACE,{"disambiguationData":[OSD([sQuery(id+"F4.wireOp",EDGE,"E33.1.0.0")])]})]}),makeQuery(id+"F8.opExtrude","SWEPT_FACE",FACE,{"disambiguationData":[OSD([sQuery(id+"F7.wireOp",EDGE,"E44.right")])]}),makeQuery(id+"F8.opExtrude","SWEPT_FACE",FACE,{"disambiguationData":[OSD([sQuery(id+"F7.wireOp",EDGE,"E54.0.1.0")])]})]});
            var sketch = newSketch(context, id + "F10", { "sketchPlane" : qUnion([Q0])});
            skLineSegment(sketch, "E73.bottom", {"start": v(-48.2, 405.62) * mm, "end": v(-15.8, 405.62) * mm});
            skLineSegment(sketch, "E73.top", {"start": v(-48.2, 444.02) * mm, "end": v(-15.8, 444.02) * mm});
            skLineSegment(sketch, "E73.left", {"start": v(-51.2, 408.62) * mm, "end": v(-51.2, 441.02) * mm});
            skLineSegment(sketch, "E73.right", {"start": v(-12.8, 408.62) * mm, "end": v(-12.8, 441.02) * mm});
            skLineSegment(sketch, "E74.0", {"start": v(-49.2, 410.62) * mm, "end": v(-49.2, 439.02) * mm});
            skLineSegment(sketch, "E74.1", {"start": v(-46.2, 407.62) * mm, "end": v(-17.8, 407.62) * mm});
            skLineSegment(sketch, "E74.2", {"start": v(-14.8, 410.62) * mm, "end": v(-14.8, 439.02) * mm});
            skLineSegment(sketch, "E74.3", {"start": v(-46.2, 442.02) * mm, "end": v(-17.8, 442.02) * mm});
            skPoint(sketch, "E75.visualSharp", {"position": v(-49.2, 442.02) * mm});
            skArc(sketch, "E75.filletArc", {"start": v(-46.2, 442.02) * mm, "mid": v(-48.32, 441.14) * mm, "end": v(-49.2, 439.02) * mm});
            skPoint(sketch, "E76.visualSharp", {"position": v(-14.8, 442.02) * mm});
            skArc(sketch, "E76.filletArc", {"start": v(-14.8, 439.02) * mm, "mid": v(-15.68, 441.14) * mm, "end": v(-17.8, 442.02) * mm});
            skPoint(sketch, "E77.visualSharp", {"position": v(-14.8, 407.62) * mm});
            skArc(sketch, "E77.filletArc", {"start": v(-17.8, 407.62) * mm, "mid": v(-15.68, 408.5) * mm, "end": v(-14.8, 410.62) * mm});
            skPoint(sketch, "E78.visualSharp", {"position": v(-49.2, 407.62) * mm});
            skArc(sketch, "E78.filletArc", {"start": v(-49.2, 410.62) * mm, "mid": v(-48.32, 408.5) * mm, "end": v(-46.2, 407.62) * mm});
            skPoint(sketch, "E79.visualSharp", {"position": v(-51.2, 444.02) * mm});
            skArc(sketch, "E79.filletArc", {"start": v(-48.2, 444.02) * mm, "mid": v(-50.32, 443.14) * mm, "end": v(-51.2, 441.02) * mm});
            skPoint(sketch, "E80.visualSharp", {"position": v(-12.8, 444.02) * mm});
            skArc(sketch, "E80.filletArc", {"start": v(-12.8, 441.02) * mm, "mid": v(-13.68, 443.14) * mm, "end": v(-15.8, 444.02) * mm});
            skPoint(sketch, "E81.visualSharp", {"position": v(-12.8, 405.62) * mm});
            skArc(sketch, "E81.filletArc", {"start": v(-15.8, 405.62) * mm, "mid": v(-13.68, 406.5) * mm, "end": v(-12.8, 408.62) * mm});
            skPoint(sketch, "E82.visualSharp", {"position": v(-51.2, 405.62) * mm});
            skArc(sketch, "E82.filletArc", {"start": v(-51.2, 408.62) * mm, "mid": v(-50.32, 406.5) * mm, "end": v(-48.2, 405.62) * mm});
            skLineSegment(sketch, "E83.1.0.0", {"start": v(1158.2, 444.02) * mm, "end": v(1190.6, 444.02) * mm});
            skArc(sketch, "E83.1.0.1", {"start": v(1193.6, 441.02) * mm, "mid": v(1192.72, 443.14) * mm, "end": v(1190.6, 444.02) * mm});
            skLineSegment(sketch, "E83.1.0.2", {"start": v(1193.6, 408.62) * mm, "end": v(1193.6, 441.02) * mm});
            skArc(sketch, "E83.1.0.3", {"start": v(1191.6, 439.02) * mm, "mid": v(1190.72, 441.14) * mm, "end": v(1188.6, 442.02) * mm});
            skLineSegment(sketch, "E83.1.0.4", {"start": v(1160.2, 442.02) * mm, "end": v(1188.6, 442.02) * mm});
            skLineSegment(sketch, "E83.1.0.5", {"start": v(1191.6, 410.62) * mm, "end": v(1191.6, 439.02) * mm});
            skArc(sketch, "E83.1.0.6", {"start": v(1160.2, 442.02) * mm, "mid": v(1158.08, 441.14) * mm, "end": v(1157.2, 439.02) * mm});
            skArc(sketch, "E83.1.0.7", {"start": v(1158.2, 444.02) * mm, "mid": v(1156.08, 443.14) * mm, "end": v(1155.2, 441.02) * mm});
            skLineSegment(sketch, "E83.1.0.8", {"start": v(1155.2, 408.62) * mm, "end": v(1155.2, 441.02) * mm});
            skLineSegment(sketch, "E83.1.0.9", {"start": v(1157.2, 410.62) * mm, "end": v(1157.2, 439.02) * mm});
            skArc(sketch, "E83.1.0.10", {"start": v(1157.2, 410.62) * mm, "mid": v(1158.08, 408.5) * mm, "end": v(1160.2, 407.62) * mm});
            skArc(sketch, "E83.1.0.11", {"start": v(1155.2, 408.62) * mm, "mid": v(1156.08, 406.5) * mm, "end": v(1158.2, 405.62) * mm});
            skLineSegment(sketch, "E83.1.0.12", {"start": v(1160.2, 407.62) * mm, "end": v(1188.6, 407.62) * mm});
            skLineSegment(sketch, "E83.1.0.13", {"start": v(1158.2, 405.62) * mm, "end": v(1190.6, 405.62) * mm});
            skArc(sketch, "E83.1.0.14", {"start": v(1190.6, 405.62) * mm, "mid": v(1192.72, 406.5) * mm, "end": v(1193.6, 408.62) * mm});
            skArc(sketch, "E83.1.0.15", {"start": v(1188.6, 407.62) * mm, "mid": v(1190.72, 408.5) * mm, "end": v(1191.6, 410.62) * mm});
            skLineSegment(sketch, "E83.2.0.0", {"start": v(2364.6, 444.02) * mm, "end": v(2397, 444.02) * mm});
            skArc(sketch, "E83.2.0.1", {"start": v(2400, 441.02) * mm, "mid": v(2399.12, 443.14) * mm, "end": v(2397, 444.02) * mm});
            skLineSegment(sketch, "E83.2.0.2", {"start": v(2400, 408.62) * mm, "end": v(2400, 441.02) * mm});
            skArc(sketch, "E83.2.0.3", {"start": v(2398, 439.02) * mm, "mid": v(2397.12, 441.14) * mm, "end": v(2395, 442.02) * mm});
            skLineSegment(sketch, "E83.2.0.4", {"start": v(2366.6, 442.02) * mm, "end": v(2395, 442.02) * mm});
            skLineSegment(sketch, "E83.2.0.5", {"start": v(2398, 410.62) * mm, "end": v(2398, 439.02) * mm});
            skArc(sketch, "E83.2.0.6", {"start": v(2366.6, 442.02) * mm, "mid": v(2364.48, 441.14) * mm, "end": v(2363.6, 439.02) * mm});
            skArc(sketch, "E83.2.0.7", {"start": v(2364.6, 444.02) * mm, "mid": v(2362.48, 443.14) * mm, "end": v(2361.6, 441.02) * mm});
            skLineSegment(sketch, "E83.2.0.8", {"start": v(2361.6, 408.62) * mm, "end": v(2361.6, 441.02) * mm});
            skLineSegment(sketch, "E83.2.0.9", {"start": v(2363.6, 410.62) * mm, "end": v(2363.6, 439.02) * mm});
            skArc(sketch, "E83.2.0.10", {"start": v(2363.6, 410.62) * mm, "mid": v(2364.48, 408.5) * mm, "end": v(2366.6, 407.62) * mm});
            skArc(sketch, "E83.2.0.11", {"start": v(2361.6, 408.62) * mm, "mid": v(2362.48, 406.5) * mm, "end": v(2364.6, 405.62) * mm});
            skLineSegment(sketch, "E83.2.0.12", {"start": v(2366.6, 407.62) * mm, "end": v(2395, 407.62) * mm});
            skLineSegment(sketch, "E83.2.0.13", {"start": v(2364.6, 405.62) * mm, "end": v(2397, 405.62) * mm});
            skArc(sketch, "E83.2.0.14", {"start": v(2397, 405.62) * mm, "mid": v(2399.12, 406.5) * mm, "end": v(2400, 408.62) * mm});
            skArc(sketch, "E83.2.0.15", {"start": v(2395, 407.62) * mm, "mid": v(2397.12, 408.5) * mm, "end": v(2398, 410.62) * mm});
            skLineSegment(sketch, "E83.direction1", {"start": v(-48.2, 444.02) * mm, "end": v(1158.2, 444.02) * mm, "construction": true});
            skSolve(sketch);
        }
        {
            var Q0;
            Q0=makeQuery(id+"F10.imprint","IMPRINT",FACE,{"disambiguationData":[TD([[makeQuery(id+"F10.imprint","IMPRINT",EDGE,{"derivedFrom":sQuery(id+"F10.wireOp",EDGE,"E73.bottom")}),1.0]])]});
            var Q1;
            Q1=makeQuery(id+"F10.imprint","IMPRINT",FACE,{"disambiguationData":[TD([[makeQuery(id+"F10.imprint","IMPRINT",EDGE,{"derivedFrom":sQuery(id+"F10.wireOp",EDGE,"E83.1.0.0")}),-1.0]])]});
            var Q2;
            Q2=makeQuery(id+"F10.imprint","IMPRINT",FACE,{"disambiguationData":[TD([[makeQuery(id+"F10.imprint","IMPRINT",EDGE,{"derivedFrom":sQuery(id+"F10.wireOp",EDGE,"E83.2.0.0")}),-1.0]])]});
            var Q3;
            Q3=sQuery(id+"F9.wireOp",EDGE,"E70.0");
            sweep(context, id + "F11", {"operationType" : NewBodyOperationType.ADD, "profiles" : qUnion([Q0, Q1, Q2]), "path" : qUnion([Q3])});
        }
        {
            var Q0;
            Q0=makeQuery(id+"F10.imprint","IMPRINT",FACE,{"disambiguationData":[TD([[makeQuery(id+"F10.imprint","IMPRINT",EDGE,{"derivedFrom":sQuery(id+"F10.wireOp",EDGE,"E73.bottom")}),1.0]])]});
            var Q1;
            Q1=makeQuery(id+"F10.imprint","IMPRINT",FACE,{"disambiguationData":[TD([[makeQuery(id+"F10.imprint","IMPRINT",EDGE,{"derivedFrom":sQuery(id+"F10.wireOp",EDGE,"E83.1.0.0")}),-1.0]])]});
            var Q2;
            Q2=makeQuery(id+"F10.imprint","IMPRINT",FACE,{"disambiguationData":[TD([[makeQuery(id+"F10.imprint","IMPRINT",EDGE,{"derivedFrom":sQuery(id+"F10.wireOp",EDGE,"E83.2.0.0")}),-1.0]])]});
            var Q3;
            Q3=sQuery(id+"F9.wireOp",EDGE,"E72");
            sweep(context, id + "F12", {"operationType" : NewBodyOperationType.ADD, "profiles" : qUnion([Q0, Q1, Q2]), "path" : qUnion([Q3])});
        }
        {
            var Q0;
            {var subQ0=sQuery(id+"F10.wireOp",EDGE,"E73.left");Q0=makeQuery(id+"F12.boolean.opBoolean","MERGE",FACE,{"derivedFrom":[makeQuery(id+"F11.opSweep","SWEPT_FACE",FACE,{"disambiguationData":[OSD([sQuery(id+"F9.wireOp",EDGE,"E70.0"),subQ0])]}),makeQuery(id+"F12.opSweep","SWEPT_FACE",FACE,{"disambiguationData":[OSD([sQuery(id+"F9.wireOp",EDGE,"E72"),subQ0])]})]});}
            var sketch = newSketch(context, id + "F13", { "sketchPlane" : qUnion([Q0])});
            skLineSegment(sketch, "E84", {"start": v(-2059.34, 32.78) * mm, "end": v(-2048.75, 34.9) * mm});
            skLineSegment(sketch, "E85", {"start": v(-2048.75, 34.9) * mm, "end": v(-2044.72, 61.2) * mm});
            skLineSegment(sketch, "E86", {"start": v(-2044.72, 61.2) * mm, "end": v(-2025.1, 65.1) * mm});
            skLineSegment(sketch, "E87", {"start": v(-2025.1, 65.1) * mm, "end": v(-2011.29, 42.38) * mm});
            skLineSegment(sketch, "E88.trimOffspring", {"start": v(-2011.29, 42.38) * mm, "end": v(-1999.52, 44.73) * mm});
            skLineSegment(sketch, "E89.0", {"start": v(-2011.58, 41.7) * mm, "end": v(-1999.4, 44.14) * mm});
            skLineSegment(sketch, "E89.1", {"start": v(-2059.22, 32.2) * mm, "end": v(-2048.22, 34.39) * mm});
            skLineSegment(sketch, "E89.2", {"start": v(-2048.22, 34.39) * mm, "end": v(-2044.2, 60.69) * mm});
            skLineSegment(sketch, "E89.3", {"start": v(-2044.2, 60.69) * mm, "end": v(-2025.4, 64.44) * mm});
            skLineSegment(sketch, "E89.4", {"start": v(-2025.4, 64.44) * mm, "end": v(-2011.58, 41.7) * mm});
            skLineSegment(sketch, "E90", {"start": v(-1999.52, 44.73) * mm, "end": v(-1999.4, 44.14) * mm});
            skLineSegment(sketch, "E91", {"start": v(-2059.34, 32.78) * mm, "end": v(-2059.22, 32.2) * mm});
            skLineSegment(sketch, "E92", {"start": v(-902.34, 263.83) * mm, "end": v(-891.75, 265.94) * mm});
            skLineSegment(sketch, "E93", {"start": v(-891.75, 265.94) * mm, "end": v(-887.73, 292.24) * mm});
            skLineSegment(sketch, "E94", {"start": v(-887.73, 292.24) * mm, "end": v(-868.11, 296.16) * mm});
            skLineSegment(sketch, "E95", {"start": v(-868.11, 296.16) * mm, "end": v(-854.3, 273.42) * mm});
            skLineSegment(sketch, "E96.trimOffspring", {"start": v(-854.3, 273.42) * mm, "end": v(-842.53, 275.77) * mm});
            skLineSegment(sketch, "E97.0", {"start": v(-854.59, 272.75) * mm, "end": v(-842.4, 275.18) * mm});
            skLineSegment(sketch, "E97.1", {"start": v(-902.23, 263.24) * mm, "end": v(-891.22, 265.44) * mm});
            skLineSegment(sketch, "E97.2", {"start": v(-891.22, 265.44) * mm, "end": v(-887.2, 291.73) * mm});
            skLineSegment(sketch, "E97.3", {"start": v(-887.2, 291.73) * mm, "end": v(-868.4, 295.49) * mm});
            skLineSegment(sketch, "E97.4", {"start": v(-868.4, 295.49) * mm, "end": v(-854.59, 272.75) * mm});
            skLineSegment(sketch, "E98", {"start": v(-842.53, 275.77) * mm, "end": v(-842.4, 275.18) * mm});
            skLineSegment(sketch, "E99", {"start": v(-902.34, 263.83) * mm, "end": v(-902.23, 263.24) * mm});
            skLineSegment(sketch, "E100", {"start": v(230.69, 490.09) * mm, "end": v(241.28, 492.2) * mm});
            skLineSegment(sketch, "E101", {"start": v(241.28, 492.2) * mm, "end": v(245.3, 518.5) * mm});
            skLineSegment(sketch, "E102", {"start": v(245.3, 518.5) * mm, "end": v(264.92, 522.42) * mm});
            skLineSegment(sketch, "E103", {"start": v(264.92, 522.42) * mm, "end": v(278.74, 499.69) * mm});
            skLineSegment(sketch, "E104.trimOffspring", {"start": v(278.74, 499.69) * mm, "end": v(290.5, 502.04) * mm});
            skLineSegment(sketch, "E105.0", {"start": v(278.44, 499.01) * mm, "end": v(290.62, 501.45) * mm});
            skLineSegment(sketch, "E105.1", {"start": v(230.8, 489.5) * mm, "end": v(241.8, 491.7) * mm});
            skLineSegment(sketch, "E105.2", {"start": v(241.8, 491.7) * mm, "end": v(245.83, 518) * mm});
            skLineSegment(sketch, "E105.3", {"start": v(245.83, 518) * mm, "end": v(264.62, 521.75) * mm});
            skLineSegment(sketch, "E105.4", {"start": v(264.62, 521.75) * mm, "end": v(278.44, 499.01) * mm});
            skLineSegment(sketch, "E106", {"start": v(290.5, 502.04) * mm, "end": v(290.62, 501.45) * mm});
            skLineSegment(sketch, "E107", {"start": v(230.69, 490.09) * mm, "end": v(230.8, 489.5) * mm});
            skLineSegment(sketch, "E108", {"start": v(-2059.34, 13.58) * mm, "end": v(294.2, 483.57) * mm});
            skSolve(sketch);
        }
        {
            var Q0;
            {var subQ0=sQuery(id+"F10.wireOp",EDGE,"E73.top");Q0=makeQuery(id+"F12.boolean.opBoolean","MERGE",FACE,{"derivedFrom":[makeQuery(id+"F11.opSweep","SWEPT_FACE",FACE,{"disambiguationData":[OSD([sQuery(id+"F9.wireOp",EDGE,"E70.0"),subQ0])]}),makeQuery(id+"F12.opSweep","SWEPT_FACE",FACE,{"disambiguationData":[OSD([sQuery(id+"F9.wireOp",EDGE,"E72"),subQ0])]})]});}
            var sketch = newSketch(context, id + "F14", { "sketchPlane" : qUnion([Q0])});
            skLineSegment(sketch, "E109", {"start": v(-51.2, 2013.05) * mm, "end": v(2600, 2013.05) * mm});
            skLineSegment(sketch, "E110", {"start": v(-51.2, 2013.05) * mm, "end": v(-251.2, 2013.05) * mm});
            skSolve(sketch);
        }
        {
            var Q0;
            Q0=makeQuery(id+"F13.imprint","IMPRINT",FACE,{"disambiguationData":[TD([[makeQuery(id+"F13.imprint","IMPRINT",EDGE,{"derivedFrom":sQuery(id+"F13.wireOp",EDGE,"E84")}),-1.0]])]});
            var Q1;
            Q1=makeQuery(id+"F13.imprint","IMPRINT",FACE,{"disambiguationData":[TD([[makeQuery(id+"F13.imprint","IMPRINT",EDGE,{"derivedFrom":sQuery(id+"F13.wireOp",EDGE,"E92")}),-1.0]])]});
            var Q2;
            Q2=makeQuery(id+"F13.imprint","IMPRINT",FACE,{"disambiguationData":[TD([[makeQuery(id+"F13.imprint","IMPRINT",EDGE,{"derivedFrom":sQuery(id+"F13.wireOp",EDGE,"E100")}),-1.0]])]});
            var Q3;
            Q3=sQuery(id+"F14.wireOp",EDGE,"E109");
            sweep(context, id + "F15", {"operationType" : NewBodyOperationType.ADD, "profiles" : qUnion([Q0, Q1, Q2]), "path" : qUnion([Q3])});
        }
        {
            var Q0;
            Q0=makeQuery(id+"F13.imprint","IMPRINT",FACE,{"disambiguationData":[TD([[makeQuery(id+"F13.imprint","IMPRINT",EDGE,{"derivedFrom":sQuery(id+"F13.wireOp",EDGE,"E84")}),-1.0]])]});
            var Q1;
            Q1=makeQuery(id+"F13.imprint","IMPRINT",FACE,{"disambiguationData":[TD([[makeQuery(id+"F13.imprint","IMPRINT",EDGE,{"derivedFrom":sQuery(id+"F13.wireOp",EDGE,"E92")}),-1.0]])]});
            var Q2;
            Q2=makeQuery(id+"F13.imprint","IMPRINT",FACE,{"disambiguationData":[TD([[makeQuery(id+"F13.imprint","IMPRINT",EDGE,{"derivedFrom":sQuery(id+"F13.wireOp",EDGE,"E100")}),-1.0]])]});
            var Q3;
            Q3=sQuery(id+"F14.wireOp",EDGE,"E110");
            sweep(context, id + "F16", {"operationType" : NewBodyOperationType.ADD, "profiles" : qUnion([Q0, Q1, Q2]), "path" : qUnion([Q3])});
        }
    });
